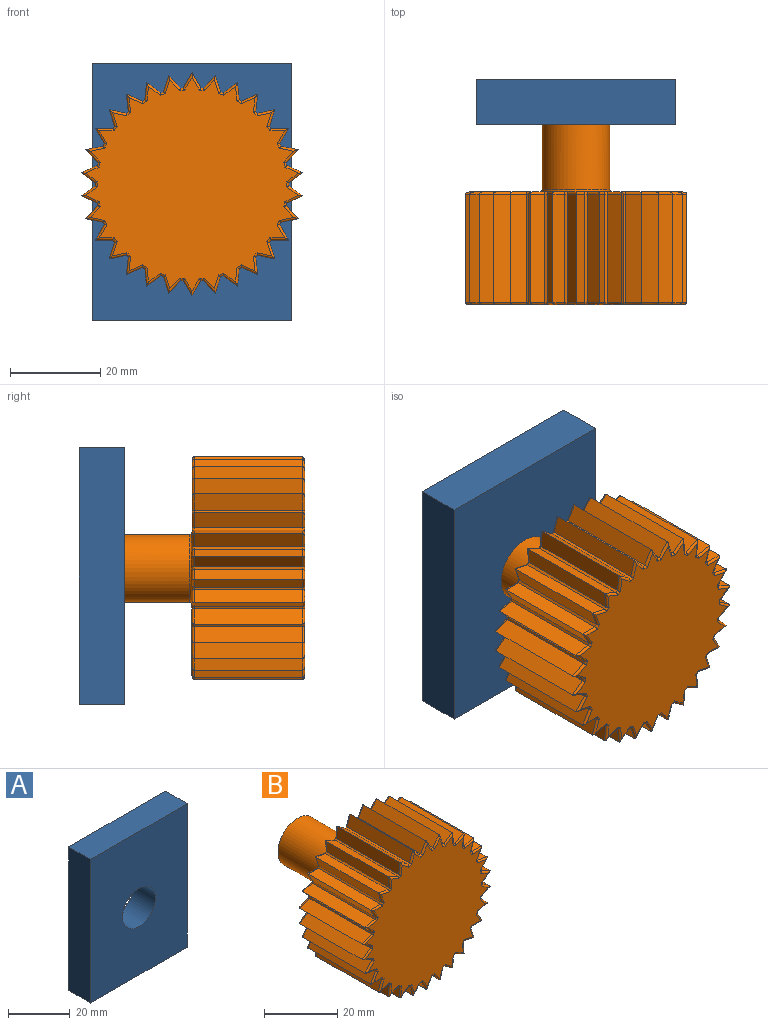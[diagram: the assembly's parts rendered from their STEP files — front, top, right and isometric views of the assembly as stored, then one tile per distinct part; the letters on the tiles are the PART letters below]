
ASSEMBLY  parts=2 mates=1
PART A: 7 faces, bbox 44.3x10x56.8 mm
  f0: plane 56.81x10mm, normal (-1,0,0), area 568.1mm2, adj f1,f4,f5,f6
  f1: plane 44.33x10mm, normal (0,0,-1), area 443.3mm2, adj f0,f2,f5,f6
  f2: plane 56.81x10mm, normal (1,0,0), area 568.1mm2, adj f1,f4,f5,f6
  f3: cylinder r=7.5mm len=15mm, axis (0,-1,0), area 471.2mm2, adj f5,f6
  f4: plane 44.33x10mm, normal (0,0,1), area 443.3mm2, adj f0,f2,f5,f6
  f5: plane 56.81x44.33mm, normal (0,1,0), area 2342mm2, adj f0,f1,f2,f3,f4
  f6: plane 56.81x44.33mm, normal (0,-1,0), area 2342mm2, adj f0,f1,f2,f3,f4
PART B: 275 faces, bbox 49.2x50x49.5 mm
  f0: plane 24x3.7mm, normal (-0.95,0,0.31), area 93.3mm2, adj f1,f89,f179,f270
  f1: plane 24x3.8mm, normal (0.21,0,-0.98), area 93.3mm2, adj f0,f2,f177,f268
  f2: plane 24x0.45mm, normal (-0.67,0,-0.74), area 14.4mm2, adj f1,f3,f175,f266
  f3: plane 24x3.87mm, normal (-0.99,0,0.1), area 93.3mm2, adj f2,f4,f173,f264
  f4: plane 24x3.55mm, normal (0.41,0,-0.91), area 93.3mm2, adj f3,f5,f171,f262
  f5: plane 24x0.52mm, normal (-0.5,0,-0.87), area 14.4mm2, adj f4,f6,f169,f260
  f6: plane 24x3.87mm, normal (-0.99,0,-0.1), area 93.3mm2, adj f5,f7,f167,f258
  f7: plane 24x3.15mm, normal (0.59,0,-0.81), area 93.3mm2, adj f6,f8,f165,f256
  f8: plane 24x0.57mm, normal (-0.31,0,-0.95), area 14.4mm2, adj f7,f9,f163,f254
  f9: plane 24x3.7mm, normal (-0.95,0,-0.31), area 93.3mm2, adj f8,f10,f161,f252
  f10: plane 24x2.89mm, normal (0.74,0,-0.67), area 93.3mm2, adj f9,f11,f159,f250
  f11: plane 24x0.6mm, normal (-0.1,0,-0.99), area 14.4mm2, adj f10,f12,f157,f248
  f12: plane 24x3.37mm, normal (-0.87,0,-0.5), area 93.3mm2, adj f11,f13,f155,f246
  f13: plane 24x3.37mm, normal (0.87,0,-0.5), area 93.3mm2, adj f12,f14,f153,f244
  f14: plane 24x0.6mm, normal (0.1,0,-0.99), area 14.4mm2, adj f13,f15,f151,f242
  f15: plane 24x2.89mm, normal (-0.74,0,-0.67), area 93.3mm2, adj f14,f16,f149,f240
  f16: plane 24x3.7mm, normal (0.95,0,-0.31), area 93.3mm2, adj f15,f17,f147,f238
  f17: plane 24x0.57mm, normal (0.31,0,-0.95), area 14.4mm2, adj f16,f18,f145,f236
  f18: plane 24x3.15mm, normal (-0.59,0,-0.81), area 93.3mm2, adj f17,f19,f143,f234
  f19: plane 24x3.87mm, normal (0.99,0,-0.1), area 93.3mm2, adj f18,f20,f141,f232
  f20: plane 24x0.52mm, normal (0.5,0,-0.87), area 14.4mm2, adj f19,f21,f139,f230
  f21: plane 24x3.55mm, normal (-0.41,0,-0.91), area 93.3mm2, adj f20,f22,f137,f228
  f22: plane 24x3.87mm, normal (0.99,0,0.1), area 93.3mm2, adj f21,f23,f135,f226
  f23: plane 24x0.45mm, normal (0.67,0,-0.74), area 14.4mm2, adj f22,f24,f133,f224
  f24: plane 24x3.8mm, normal (-0.21,0,-0.98), area 93.3mm2, adj f23,f25,f131,f222
  f25: plane 24x3.7mm, normal (0.95,0,0.31), area 93.3mm2, adj f24,f26,f129,f220
  f26: plane 24x0.48mm, normal (0.81,0,-0.59), area 14.4mm2, adj f25,f27,f127,f218
  f27: plane 24x3.89mm, normal (0,0,-1), area 93.3mm2, adj f26,f28,f125,f216
  f28: plane 24x3.37mm, normal (0.87,0,0.5), area 93.3mm2, adj f27,f29,f123,f214
  f29: plane 24x0.55mm, normal (0.91,0,-0.41), area 14.4mm2, adj f28,f30,f121,f212
  f30: plane 24x3.8mm, normal (0.21,0,-0.98), area 93.3mm2, adj f29,f31,f119,f210
  f31: plane 24x2.89mm, normal (0.74,0,0.67), area 93.3mm2, adj f30,f32,f117,f208
  f32: plane 24x0.59mm, normal (0.98,0,-0.21), area 14.4mm2, adj f31,f33,f115,f206
  f33: plane 24x3.55mm, normal (0.41,0,-0.91), area 93.3mm2, adj f32,f34,f113,f204
  f34: plane 24x3.15mm, normal (0.59,0,0.81), area 93.3mm2, adj f33,f35,f111,f202
  f35: plane 24x0.6mm, normal (1,0,0), area 14.4mm2, adj f34,f36,f109,f200
  f36: plane 24x3.15mm, normal (0.59,0,-0.81), area 93.3mm2, adj f35,f37,f107,f198
  f37: plane 24x3.55mm, normal (0.41,0,0.91), area 93.3mm2, adj f36,f38,f105,f196
  f38: plane 24x0.59mm, normal (0.98,0,0.21), area 14.4mm2, adj f37,f39,f103,f194
  f39: plane 24x2.89mm, normal (0.74,0,-0.67), area 93.3mm2, adj f38,f40,f101,f192
  f40: plane 24x3.8mm, normal (0.21,0,0.98), area 93.3mm2, adj f39,f41,f99,f190
  f41: plane 24x0.55mm, normal (0.91,0,0.41), area 14.4mm2, adj f40,f42,f97,f188
  f42: plane 24x3.37mm, normal (0.87,0,-0.5), area 93.3mm2, adj f41,f43,f95,f186
  f43: plane 24x3.89mm, normal (0,0,1), area 93.3mm2, adj f42,f44,f94,f185
  f44: plane 24x0.48mm, normal (0.81,0,0.59), area 14.4mm2, adj f43,f45,f96,f187
  f45: plane 24x3.7mm, normal (0.95,0,-0.31), area 93.3mm2, adj f44,f46,f98,f189
  f46: plane 24x3.8mm, normal (-0.21,0,0.98), area 93.3mm2, adj f45,f47,f100,f191
  f47: plane 24x0.45mm, normal (0.67,0,0.74), area 14.4mm2, adj f46,f48,f102,f193
  f48: plane 24x3.87mm, normal (0.99,0,-0.1), area 93.3mm2, adj f47,f49,f104,f195
  f49: plane 24x3.55mm, normal (-0.41,0,0.91), area 93.3mm2, adj f48,f50,f106,f197
  f50: plane 24x0.52mm, normal (0.5,0,0.87), area 14.4mm2, adj f49,f51,f108,f199
  f51: plane 24x3.87mm, normal (0.99,0,0.1), area 93.3mm2, adj f50,f52,f110,f201
  f52: plane 24x3.15mm, normal (-0.59,0,0.81), area 93.3mm2, adj f51,f53,f112,f203
  f53: plane 24x0.57mm, normal (0.31,0,0.95), area 14.4mm2, adj f52,f54,f114,f205
  f54: plane 24x3.7mm, normal (0.95,0,0.31), area 93.3mm2, adj f53,f55,f116,f207
  f55: plane 24x2.89mm, normal (-0.74,0,0.67), area 93.3mm2, adj f54,f56,f118,f209
  f56: plane 24x0.6mm, normal (0.1,0,0.99), area 14.4mm2, adj f55,f57,f120,f211
  f57: plane 24x3.37mm, normal (0.87,0,0.5), area 93.3mm2, adj f56,f58,f122,f213
  f58: plane 24x3.37mm, normal (-0.87,0,0.5), area 93.3mm2, adj f57,f59,f124,f215
  f59: plane 24x0.6mm, normal (-0.1,0,0.99), area 14.4mm2, adj f58,f60,f126,f217
  f60: plane 24x2.89mm, normal (0.74,0,0.67), area 93.3mm2, adj f59,f61,f128,f219
  f61: plane 24x3.7mm, normal (-0.95,0,0.31), area 93.3mm2, adj f60,f62,f130,f221
  f62: plane 24x0.57mm, normal (-0.31,0,0.95), area 14.4mm2, adj f61,f63,f132,f223
  f63: plane 24x3.15mm, normal (0.59,0,0.81), area 93.3mm2, adj f62,f64,f134,f225
  f64: plane 24x3.87mm, normal (-0.99,0,0.1), area 93.3mm2, adj f63,f65,f136,f227
  f65: plane 24x0.52mm, normal (-0.5,0,0.87), area 14.4mm2, adj f64,f66,f138,f229
  f66: plane 24x3.55mm, normal (0.41,0,0.91), area 93.3mm2, adj f65,f67,f140,f231
  f67: plane 24x3.87mm, normal (-0.99,0,-0.1), area 93.3mm2, adj f66,f68,f142,f233
  f68: plane 24x0.45mm, normal (-0.67,0,0.74), area 14.4mm2, adj f67,f69,f144,f235
  f69: plane 24x3.8mm, normal (0.21,0,0.98), area 93.3mm2, adj f68,f70,f146,f237
  f70: plane 24x3.7mm, normal (-0.95,0,-0.31), area 93.3mm2, adj f69,f71,f148,f239
  f71: plane 24x0.48mm, normal (-0.81,0,0.59), area 14.4mm2, adj f70,f72,f150,f241
  f72: plane 24x3.89mm, normal (0,0,1), area 93.3mm2, adj f71,f73,f152,f243
  f73: plane 24x3.37mm, normal (-0.87,0,-0.5), area 93.3mm2, adj f72,f74,f154,f245
  f74: plane 24x0.55mm, normal (-0.91,0,0.41), area 14.4mm2, adj f73,f75,f156,f247
  f75: plane 24x3.8mm, normal (-0.21,0,0.98), area 93.3mm2, adj f74,f76,f158,f249
  f76: plane 24x2.89mm, normal (-0.74,0,-0.67), area 93.3mm2, adj f75,f77,f160,f251
  f77: plane 24x0.59mm, normal (-0.98,0,0.21), area 14.4mm2, adj f76,f78,f162,f253
  f78: plane 24x3.55mm, normal (-0.41,0,0.91), area 93.3mm2, adj f77,f79,f164,f255
  f79: plane 24x3.15mm, normal (-0.59,0,-0.81), area 93.3mm2, adj f78,f80,f166,f257
  f80: plane 24x0.6mm, normal (-1,0,0), area 14.4mm2, adj f79,f81,f168,f259
  f81: plane 24x3.15mm, normal (-0.59,0,0.81), area 93.3mm2, adj f80,f82,f170,f261
  f82: plane 24x3.55mm, normal (-0.41,0,-0.91), area 93.3mm2, adj f81,f83,f172,f263
  f83: plane 24x0.59mm, normal (-0.98,0,-0.21), area 14.4mm2, adj f82,f84,f174,f265
  f84: plane 24x2.89mm, normal (-0.74,0,0.67), area 93.3mm2, adj f83,f85,f176,f267
  f85: plane 24x3.8mm, normal (-0.21,0,-0.98), area 93.3mm2, adj f84,f86,f178,f269
  f86: plane 24x0.55mm, normal (-0.91,0,-0.41), area 14.4mm2, adj f85,f87,f180,f271
  f87: plane 24x3.37mm, normal (-0.87,0,0.5), area 93.3mm2, adj f86,f88,f182,f273
  f88: plane 24x3.89mm, normal (0,0,-1), area 93.3mm2, adj f87,f89,f183,f274
  f89: plane 24x0.48mm, normal (-0.81,0,-0.59), area 14.4mm2, adj f0,f88,f181,f272
  f90: plane 47.47x47.21mm, normal (0,-1,0), area 1515.3mm2, adj f94,f95,f96,f97,f98,f99,f100,f101
  f91: plane 47.47x47.21mm, normal (0,1,0), area 1314.3mm2, adj f184,f185,f186,f187,f188,f189,f190,f191
  f92: cylinder r=7.5mm len=24.5mm, axis (0,1,0), area 1154.5mm2, adj f93,f184
  f93: plane 15x15mm, normal (0,1,0), area 176.7mm2, adj f92
  f94: cylinder r=0.5mm len=4.14mm, axis (1,0,0), area 2.9mm2, adj f43,f90,f95,f96
  f95: cylinder r=0.5mm len=3.84mm, axis (-0.5,0,-0.87), area 2.9mm2, adj f42,f90,f94,f97
  f96: cylinder r=0.5mm len=1.19mm, axis (0.59,0,-0.81), area 0.6mm2, adj f44,f90,f94,f98
  f97: cylinder r=0.5mm len=1.22mm, axis (0.41,0,-0.91), area 0.6mm2, adj f41,f90,f95,f99
  f98: cylinder r=0.5mm len=4.1mm, axis (-0.31,0,-0.95), area 2.9mm2, adj f45,f90,f96,f100
  f99: cylinder r=0.5mm len=4.16mm, axis (0.98,0,-0.21), area 2.9mm2, adj f40,f90,f97,f101
  f100: cylinder r=0.5mm len=4.16mm, axis (0.98,0,0.21), area 2.9mm2, adj f46,f90,f98,f102
  f101: cylinder r=0.5mm len=3.41mm, axis (-0.67,0,-0.74), area 2.9mm2, adj f39,f90,f99,f103
  f102: cylinder r=0.5mm len=1.16mm, axis (0.74,0,-0.67), area 0.6mm2, adj f47,f90,f100,f104
  f103: cylinder r=0.5mm len=1.19mm, axis (0.21,0,-0.98), area 0.6mm2, adj f38,f90,f101,f105
  f104: cylinder r=0.5mm len=4.17mm, axis (-0.1,0,-0.99), area 2.9mm2, adj f48,f90,f102,f106
  f105: cylinder r=0.5mm len=3.99mm, axis (0.91,0,-0.41), area 2.9mm2, adj f37,f90,f103,f107
  f106: cylinder r=0.5mm len=3.99mm, axis (0.91,0,0.41), area 2.9mm2, adj f49,f90,f104,f108
  f107: cylinder r=0.5mm len=3.65mm, axis (-0.81,0,-0.59), area 2.9mm2, adj f36,f90,f105,f109
  f108: cylinder r=0.5mm len=1.21mm, axis (0.87,0,-0.5), area 0.6mm2, adj f50,f90,f106,f110
  f109: cylinder r=0.5mm len=1.11mm, axis (0,0,-1), area 0.6mm2, adj f35,f90,f107,f111
  f110: cylinder r=0.5mm len=4.17mm, axis (0.1,0,-0.99), area 2.9mm2, adj f51,f90,f108,f112
  f111: cylinder r=0.5mm len=3.65mm, axis (0.81,0,-0.59), area 2.9mm2, adj f34,f90,f109,f113
  f112: cylinder r=0.5mm len=3.65mm, axis (0.81,0,0.59), area 2.9mm2, adj f52,f90,f110,f114
  f113: cylinder r=0.5mm len=3.99mm, axis (-0.91,0,-0.41), area 2.9mm2, adj f33,f90,f111,f115
  f114: cylinder r=0.5mm len=1.21mm, axis (0.95,0,-0.31), area 0.6mm2, adj f53,f90,f112,f116
  f115: cylinder r=0.5mm len=1.19mm, axis (-0.21,0,-0.98), area 0.6mm2, adj f32,f90,f113,f117
  f116: cylinder r=0.5mm len=4.1mm, axis (0.31,0,-0.95), area 2.9mm2, adj f54,f90,f114,f118
  f117: cylinder r=0.5mm len=3.41mm, axis (0.67,0,-0.74), area 2.9mm2, adj f31,f90,f115,f119
  f118: cylinder r=0.5mm len=3.41mm, axis (0.67,0,0.74), area 2.9mm2, adj f55,f90,f116,f120
  f119: cylinder r=0.5mm len=4.16mm, axis (-0.98,0,-0.21), area 2.9mm2, adj f30,f90,f117,f121
  f120: cylinder r=0.5mm len=1.15mm, axis (0.99,0,-0.1), area 0.6mm2, adj f56,f90,f118,f122
  f121: cylinder r=0.5mm len=1.22mm, axis (-0.41,0,-0.91), area 0.6mm2, adj f29,f90,f119,f123
  f122: cylinder r=0.5mm len=3.84mm, axis (0.5,0,-0.87), area 2.9mm2, adj f57,f90,f120,f124
  f123: cylinder r=0.5mm len=3.84mm, axis (0.5,0,-0.87), area 2.9mm2, adj f28,f90,f121,f125
  f124: cylinder r=0.5mm len=3.84mm, axis (0.5,0,0.87), area 2.9mm2, adj f58,f90,f122,f126
  f125: cylinder r=0.5mm len=4.14mm, axis (-1,0,0), area 2.9mm2, adj f27,f90,f123,f127
  f126: cylinder r=0.5mm len=1.15mm, axis (0.99,0,0.1), area 0.6mm2, adj f59,f90,f124,f128
  f127: cylinder r=0.5mm len=1.19mm, axis (-0.59,0,-0.81), area 0.6mm2, adj f26,f90,f125,f129
  f128: cylinder r=0.5mm len=3.41mm, axis (0.67,0,-0.74), area 2.9mm2, adj f60,f90,f126,f130
  f129: cylinder r=0.5mm len=4.1mm, axis (0.31,0,-0.95), area 2.9mm2, adj f25,f90,f127,f131
  f130: cylinder r=0.5mm len=4.1mm, axis (0.31,0,0.95), area 2.9mm2, adj f61,f90,f128,f132
  f131: cylinder r=0.5mm len=4.16mm, axis (-0.98,0,0.21), area 2.9mm2, adj f24,f90,f129,f133
  f132: cylinder r=0.5mm len=1.21mm, axis (0.95,0,0.31), area 0.6mm2, adj f62,f90,f130,f134
  f133: cylinder r=0.5mm len=1.16mm, axis (-0.74,0,-0.67), area 0.6mm2, adj f23,f90,f131,f135
  f134: cylinder r=0.5mm len=3.65mm, axis (0.81,0,-0.59), area 2.9mm2, adj f63,f90,f132,f136
  f135: cylinder r=0.5mm len=4.17mm, axis (0.1,0,-0.99), area 2.9mm2, adj f22,f90,f133,f137
  f136: cylinder r=0.5mm len=4.17mm, axis (0.1,0,0.99), area 2.9mm2, adj f64,f90,f134,f138
  f137: cylinder r=0.5mm len=3.99mm, axis (-0.91,0,0.41), area 2.9mm2, adj f21,f90,f135,f139
  f138: cylinder r=0.5mm len=1.21mm, axis (0.87,0,0.5), area 0.6mm2, adj f65,f90,f136,f140
  f139: cylinder r=0.5mm len=1.21mm, axis (-0.87,0,-0.5), area 0.6mm2, adj f20,f90,f137,f141
  f140: cylinder r=0.5mm len=3.99mm, axis (0.91,0,-0.41), area 2.9mm2, adj f66,f90,f138,f142
  f141: cylinder r=0.5mm len=4.17mm, axis (-0.1,0,-0.99), area 2.9mm2, adj f19,f90,f139,f143
  f142: cylinder r=0.5mm len=4.17mm, axis (-0.1,0,0.99), area 2.9mm2, adj f67,f90,f140,f144
  f143: cylinder r=0.5mm len=3.65mm, axis (-0.81,0,0.59), area 2.9mm2, adj f18,f90,f141,f145
  f144: cylinder r=0.5mm len=1.16mm, axis (0.74,0,0.67), area 0.6mm2, adj f68,f90,f142,f146
  f145: cylinder r=0.5mm len=1.21mm, axis (-0.95,0,-0.31), area 0.6mm2, adj f17,f90,f143,f147
  f146: cylinder r=0.5mm len=4.16mm, axis (0.98,0,-0.21), area 2.9mm2, adj f69,f90,f144,f148
  f147: cylinder r=0.5mm len=4.1mm, axis (-0.31,0,-0.95), area 2.9mm2, adj f16,f90,f145,f149
  f148: cylinder r=0.5mm len=4.1mm, axis (-0.31,0,0.95), area 2.9mm2, adj f70,f90,f146,f150
  f149: cylinder r=0.5mm len=3.41mm, axis (-0.67,0,0.74), area 2.9mm2, adj f15,f90,f147,f151
  f150: cylinder r=0.5mm len=1.19mm, axis (0.59,0,0.81), area 0.6mm2, adj f71,f90,f148,f152
  f151: cylinder r=0.5mm len=1.15mm, axis (-0.99,0,-0.1), area 0.6mm2, adj f14,f90,f149,f153
  f152: cylinder r=0.5mm len=4.14mm, axis (1,0,0), area 2.9mm2, adj f72,f90,f150,f154
  f153: cylinder r=0.5mm len=3.84mm, axis (-0.5,0,-0.87), area 2.9mm2, adj f13,f90,f151,f155
  f154: cylinder r=0.5mm len=3.84mm, axis (-0.5,0,0.87), area 2.9mm2, adj f73,f90,f152,f156
  f155: cylinder r=0.5mm len=3.84mm, axis (-0.5,0,0.87), area 2.9mm2, adj f12,f90,f153,f157
  f156: cylinder r=0.5mm len=1.22mm, axis (0.41,0,0.91), area 0.6mm2, adj f74,f90,f154,f158
  f157: cylinder r=0.5mm len=1.15mm, axis (-0.99,0,0.1), area 0.6mm2, adj f11,f90,f155,f159
  f158: cylinder r=0.5mm len=4.16mm, axis (0.98,0,0.21), area 2.9mm2, adj f75,f90,f156,f160
  f159: cylinder r=0.5mm len=3.41mm, axis (-0.67,0,-0.74), area 2.9mm2, adj f10,f90,f157,f161
  f160: cylinder r=0.5mm len=3.41mm, axis (-0.67,0,0.74), area 2.9mm2, adj f76,f90,f158,f162
  f161: cylinder r=0.5mm len=4.1mm, axis (-0.31,0,0.95), area 2.9mm2, adj f9,f90,f159,f163
  f162: cylinder r=0.5mm len=1.19mm, axis (0.21,0,0.98), area 0.6mm2, adj f77,f90,f160,f164
  f163: cylinder r=0.5mm len=1.21mm, axis (-0.95,0,0.31), area 0.6mm2, adj f8,f90,f161,f165
  f164: cylinder r=0.5mm len=3.99mm, axis (0.91,0,0.41), area 2.9mm2, adj f78,f90,f162,f166
  f165: cylinder r=0.5mm len=3.65mm, axis (-0.81,0,-0.59), area 2.9mm2, adj f7,f90,f163,f167
  f166: cylinder r=0.5mm len=3.65mm, axis (-0.81,0,0.59), area 2.9mm2, adj f79,f90,f164,f168
  f167: cylinder r=0.5mm len=4.17mm, axis (-0.1,0,0.99), area 2.9mm2, adj f6,f90,f165,f169
  f168: cylinder r=0.5mm len=1.11mm, axis (0,0,1), area 0.6mm2, adj f80,f90,f166,f170
  f169: cylinder r=0.5mm len=1.21mm, axis (-0.87,0,0.5), area 0.6mm2, adj f5,f90,f167,f171
  f170: cylinder r=0.5mm len=3.65mm, axis (0.81,0,0.59), area 2.9mm2, adj f81,f90,f168,f172
  f171: cylinder r=0.5mm len=3.99mm, axis (-0.91,0,-0.41), area 2.9mm2, adj f4,f90,f169,f173
  f172: cylinder r=0.5mm len=3.99mm, axis (-0.91,0,0.41), area 2.9mm2, adj f82,f90,f170,f174
  f173: cylinder r=0.5mm len=4.17mm, axis (0.1,0,0.99), area 2.9mm2, adj f3,f90,f171,f175
  f174: cylinder r=0.5mm len=1.19mm, axis (-0.21,0,0.98), area 0.6mm2, adj f83,f90,f172,f176
  f175: cylinder r=0.5mm len=1.16mm, axis (-0.74,0,0.67), area 0.6mm2, adj f2,f90,f173,f177
  f176: cylinder r=0.5mm len=3.41mm, axis (0.67,0,0.74), area 2.9mm2, adj f84,f90,f174,f178
  f177: cylinder r=0.5mm len=4.16mm, axis (-0.98,0,-0.21), area 2.9mm2, adj f1,f90,f175,f179
  f178: cylinder r=0.5mm len=4.16mm, axis (-0.98,0,0.21), area 2.9mm2, adj f85,f90,f176,f180
  f179: cylinder r=0.5mm len=4.1mm, axis (0.31,0,0.95), area 2.9mm2, adj f0,f90,f177,f181
  f180: cylinder r=0.5mm len=1.22mm, axis (-0.41,0,0.91), area 0.6mm2, adj f86,f90,f178,f182
  f181: cylinder r=0.5mm len=1.19mm, axis (-0.59,0,0.81), area 0.6mm2, adj f89,f90,f179,f183
  f182: cylinder r=0.5mm len=3.84mm, axis (0.5,0,0.87), area 2.9mm2, adj f87,f90,f180,f183
  f183: cylinder r=0.5mm len=4.14mm, axis (-1,0,0), area 2.9mm2, adj f88,f90,f181,f182
  f184: torus R=8mm, axis (0,-1,0), area 37.9mm2, adj f91,f92
  f185: cylinder r=0.5mm len=4.14mm, axis (-1,0,0), area 2.9mm2, adj f43,f91,f186,f187
  f186: cylinder r=0.5mm len=3.84mm, axis (0.5,0,0.87), area 2.9mm2, adj f42,f91,f185,f188
  f187: cylinder r=0.5mm len=1.19mm, axis (-0.59,0,0.81), area 0.6mm2, adj f44,f91,f185,f189
  f188: cylinder r=0.5mm len=1.22mm, axis (-0.41,0,0.91), area 0.6mm2, adj f41,f91,f186,f190
  f189: cylinder r=0.5mm len=4.1mm, axis (0.31,0,0.95), area 2.9mm2, adj f45,f91,f187,f191
  f190: cylinder r=0.5mm len=4.16mm, axis (-0.98,0,0.21), area 2.9mm2, adj f40,f91,f188,f192
  f191: cylinder r=0.5mm len=4.16mm, axis (-0.98,0,-0.21), area 2.9mm2, adj f46,f91,f189,f193
  f192: cylinder r=0.5mm len=3.41mm, axis (0.67,0,0.74), area 2.9mm2, adj f39,f91,f190,f194
  f193: cylinder r=0.5mm len=1.16mm, axis (-0.74,0,0.67), area 0.6mm2, adj f47,f91,f191,f195
  f194: cylinder r=0.5mm len=1.19mm, axis (-0.21,0,0.98), area 0.6mm2, adj f38,f91,f192,f196
  f195: cylinder r=0.5mm len=4.17mm, axis (0.1,0,0.99), area 2.9mm2, adj f48,f91,f193,f197
  f196: cylinder r=0.5mm len=3.99mm, axis (-0.91,0,0.41), area 2.9mm2, adj f37,f91,f194,f198
  f197: cylinder r=0.5mm len=3.99mm, axis (-0.91,0,-0.41), area 2.9mm2, adj f49,f91,f195,f199
  f198: cylinder r=0.5mm len=3.65mm, axis (0.81,0,0.59), area 2.9mm2, adj f36,f91,f196,f200
  f199: cylinder r=0.5mm len=1.21mm, axis (-0.87,0,0.5), area 0.6mm2, adj f50,f91,f197,f201
  f200: cylinder r=0.5mm len=1.11mm, axis (0,0,1), area 0.6mm2, adj f35,f91,f198,f202
  f201: cylinder r=0.5mm len=4.17mm, axis (-0.1,0,0.99), area 2.9mm2, adj f51,f91,f199,f203
  f202: cylinder r=0.5mm len=3.65mm, axis (-0.81,0,0.59), area 2.9mm2, adj f34,f91,f200,f204
  f203: cylinder r=0.5mm len=3.65mm, axis (-0.81,0,-0.59), area 2.9mm2, adj f52,f91,f201,f205
  f204: cylinder r=0.5mm len=3.99mm, axis (0.91,0,0.41), area 2.9mm2, adj f33,f91,f202,f206
  f205: cylinder r=0.5mm len=1.21mm, axis (-0.95,0,0.31), area 0.6mm2, adj f53,f91,f203,f207
  f206: cylinder r=0.5mm len=1.19mm, axis (0.21,0,0.98), area 0.6mm2, adj f32,f91,f204,f208
  f207: cylinder r=0.5mm len=4.1mm, axis (-0.31,0,0.95), area 2.9mm2, adj f54,f91,f205,f209
  f208: cylinder r=0.5mm len=3.41mm, axis (-0.67,0,0.74), area 2.9mm2, adj f31,f91,f206,f210
  f209: cylinder r=0.5mm len=3.41mm, axis (-0.67,0,-0.74), area 2.9mm2, adj f55,f91,f207,f211
  f210: cylinder r=0.5mm len=4.16mm, axis (0.98,0,0.21), area 2.9mm2, adj f30,f91,f208,f212
  f211: cylinder r=0.5mm len=1.15mm, axis (-0.99,0,0.1), area 0.6mm2, adj f56,f91,f209,f213
  f212: cylinder r=0.5mm len=1.22mm, axis (0.41,0,0.91), area 0.6mm2, adj f29,f91,f210,f214
  f213: cylinder r=0.5mm len=3.84mm, axis (-0.5,0,0.87), area 2.9mm2, adj f57,f91,f211,f215
  f214: cylinder r=0.5mm len=3.84mm, axis (-0.5,0,0.87), area 2.9mm2, adj f28,f91,f212,f216
  f215: cylinder r=0.5mm len=3.84mm, axis (-0.5,0,-0.87), area 2.9mm2, adj f58,f91,f213,f217
  f216: cylinder r=0.5mm len=4.14mm, axis (1,0,0), area 2.9mm2, adj f27,f91,f214,f218
  f217: cylinder r=0.5mm len=1.15mm, axis (-0.99,0,-0.1), area 0.6mm2, adj f59,f91,f215,f219
  f218: cylinder r=0.5mm len=1.19mm, axis (0.59,0,0.81), area 0.6mm2, adj f26,f91,f216,f220
  f219: cylinder r=0.5mm len=3.41mm, axis (-0.67,0,0.74), area 2.9mm2, adj f60,f91,f217,f221
  f220: cylinder r=0.5mm len=4.1mm, axis (-0.31,0,0.95), area 2.9mm2, adj f25,f91,f218,f222
  f221: cylinder r=0.5mm len=4.1mm, axis (-0.31,0,-0.95), area 2.9mm2, adj f61,f91,f219,f223
  f222: cylinder r=0.5mm len=4.16mm, axis (0.98,0,-0.21), area 2.9mm2, adj f24,f91,f220,f224
  f223: cylinder r=0.5mm len=1.21mm, axis (-0.95,0,-0.31), area 0.6mm2, adj f62,f91,f221,f225
  f224: cylinder r=0.5mm len=1.16mm, axis (0.74,0,0.67), area 0.6mm2, adj f23,f91,f222,f226
  f225: cylinder r=0.5mm len=3.65mm, axis (-0.81,0,0.59), area 2.9mm2, adj f63,f91,f223,f227
  f226: cylinder r=0.5mm len=4.17mm, axis (-0.1,0,0.99), area 2.9mm2, adj f22,f91,f224,f228
  f227: cylinder r=0.5mm len=4.17mm, axis (-0.1,0,-0.99), area 2.9mm2, adj f64,f91,f225,f229
  f228: cylinder r=0.5mm len=3.99mm, axis (0.91,0,-0.41), area 2.9mm2, adj f21,f91,f226,f230
  f229: cylinder r=0.5mm len=1.21mm, axis (-0.87,0,-0.5), area 0.6mm2, adj f65,f91,f227,f231
  f230: cylinder r=0.5mm len=1.21mm, axis (0.87,0,0.5), area 0.6mm2, adj f20,f91,f228,f232
  f231: cylinder r=0.5mm len=3.99mm, axis (-0.91,0,0.41), area 2.9mm2, adj f66,f91,f229,f233
  f232: cylinder r=0.5mm len=4.17mm, axis (0.1,0,0.99), area 2.9mm2, adj f19,f91,f230,f234
  f233: cylinder r=0.5mm len=4.17mm, axis (0.1,0,-0.99), area 2.9mm2, adj f67,f91,f231,f235
  f234: cylinder r=0.5mm len=3.65mm, axis (0.81,0,-0.59), area 2.9mm2, adj f18,f91,f232,f236
  f235: cylinder r=0.5mm len=1.16mm, axis (-0.74,0,-0.67), area 0.6mm2, adj f68,f91,f233,f237
  f236: cylinder r=0.5mm len=1.21mm, axis (0.95,0,0.31), area 0.6mm2, adj f17,f91,f234,f238
  f237: cylinder r=0.5mm len=4.16mm, axis (-0.98,0,0.21), area 2.9mm2, adj f69,f91,f235,f239
  f238: cylinder r=0.5mm len=4.1mm, axis (0.31,0,0.95), area 2.9mm2, adj f16,f91,f236,f240
  f239: cylinder r=0.5mm len=4.1mm, axis (0.31,0,-0.95), area 2.9mm2, adj f70,f91,f237,f241
  f240: cylinder r=0.5mm len=3.41mm, axis (0.67,0,-0.74), area 2.9mm2, adj f15,f91,f238,f242
  f241: cylinder r=0.5mm len=1.19mm, axis (-0.59,0,-0.81), area 0.6mm2, adj f71,f91,f239,f243
  f242: cylinder r=0.5mm len=1.15mm, axis (0.99,0,0.1), area 0.6mm2, adj f14,f91,f240,f244
  f243: cylinder r=0.5mm len=4.14mm, axis (-1,0,0), area 2.9mm2, adj f72,f91,f241,f245
  f244: cylinder r=0.5mm len=3.84mm, axis (0.5,0,0.87), area 2.9mm2, adj f13,f91,f242,f246
  f245: cylinder r=0.5mm len=3.84mm, axis (0.5,0,-0.87), area 2.9mm2, adj f73,f91,f243,f247
  f246: cylinder r=0.5mm len=3.84mm, axis (0.5,0,-0.87), area 2.9mm2, adj f12,f91,f244,f248
  f247: cylinder r=0.5mm len=1.22mm, axis (-0.41,0,-0.91), area 0.6mm2, adj f74,f91,f245,f249
  f248: cylinder r=0.5mm len=1.15mm, axis (0.99,0,-0.1), area 0.6mm2, adj f11,f91,f246,f250
  f249: cylinder r=0.5mm len=4.16mm, axis (-0.98,0,-0.21), area 2.9mm2, adj f75,f91,f247,f251
  f250: cylinder r=0.5mm len=3.41mm, axis (0.67,0,0.74), area 2.9mm2, adj f10,f91,f248,f252
  f251: cylinder r=0.5mm len=3.41mm, axis (0.67,0,-0.74), area 2.9mm2, adj f76,f91,f249,f253
  f252: cylinder r=0.5mm len=4.1mm, axis (0.31,0,-0.95), area 2.9mm2, adj f9,f91,f250,f254
  f253: cylinder r=0.5mm len=1.19mm, axis (-0.21,0,-0.98), area 0.6mm2, adj f77,f91,f251,f255
  f254: cylinder r=0.5mm len=1.21mm, axis (0.95,0,-0.31), area 0.6mm2, adj f8,f91,f252,f256
  f255: cylinder r=0.5mm len=3.99mm, axis (-0.91,0,-0.41), area 2.9mm2, adj f78,f91,f253,f257
  f256: cylinder r=0.5mm len=3.65mm, axis (0.81,0,0.59), area 2.9mm2, adj f7,f91,f254,f258
  f257: cylinder r=0.5mm len=3.65mm, axis (0.81,0,-0.59), area 2.9mm2, adj f79,f91,f255,f259
  f258: cylinder r=0.5mm len=4.17mm, axis (0.1,0,-0.99), area 2.9mm2, adj f6,f91,f256,f260
  f259: cylinder r=0.5mm len=1.11mm, axis (0,0,-1), area 0.6mm2, adj f80,f91,f257,f261
  f260: cylinder r=0.5mm len=1.21mm, axis (0.87,0,-0.5), area 0.6mm2, adj f5,f91,f258,f262
  f261: cylinder r=0.5mm len=3.65mm, axis (-0.81,0,-0.59), area 2.9mm2, adj f81,f91,f259,f263
  f262: cylinder r=0.5mm len=3.99mm, axis (0.91,0,0.41), area 2.9mm2, adj f4,f91,f260,f264
  f263: cylinder r=0.5mm len=3.99mm, axis (0.91,0,-0.41), area 2.9mm2, adj f82,f91,f261,f265
  f264: cylinder r=0.5mm len=4.17mm, axis (-0.1,0,-0.99), area 2.9mm2, adj f3,f91,f262,f266
  f265: cylinder r=0.5mm len=1.19mm, axis (0.21,0,-0.98), area 0.6mm2, adj f83,f91,f263,f267
  f266: cylinder r=0.5mm len=1.16mm, axis (0.74,0,-0.67), area 0.6mm2, adj f2,f91,f264,f268
  f267: cylinder r=0.5mm len=3.41mm, axis (-0.67,0,-0.74), area 2.9mm2, adj f84,f91,f265,f269
  f268: cylinder r=0.5mm len=4.16mm, axis (0.98,0,0.21), area 2.9mm2, adj f1,f91,f266,f270
  f269: cylinder r=0.5mm len=4.16mm, axis (0.98,0,-0.21), area 2.9mm2, adj f85,f91,f267,f271
  f270: cylinder r=0.5mm len=4.1mm, axis (-0.31,0,-0.95), area 2.9mm2, adj f0,f91,f268,f272
  f271: cylinder r=0.5mm len=1.22mm, axis (0.41,0,-0.91), area 0.6mm2, adj f86,f91,f269,f273
  f272: cylinder r=0.5mm len=1.19mm, axis (0.59,0,-0.81), area 0.6mm2, adj f89,f91,f270,f274
  f273: cylinder r=0.5mm len=3.84mm, axis (-0.5,0,-0.87), area 2.9mm2, adj f87,f91,f271,f274
  f274: cylinder r=0.5mm len=4.14mm, axis (1,0,0), area 2.9mm2, adj f88,f91,f272,f273
PLACE A rot(axis=(0,-1,0),180deg) t=(-25.3,19.82,13.72)mm fixed
PLACE B rot(axis=(0,-1,0),180deg) t=(-25.3,4.82,13.72)mm
MATE fastened B.f92 <-> A.f3  axis (0,1,0) through (-25.3,29.82,13.72)mm
